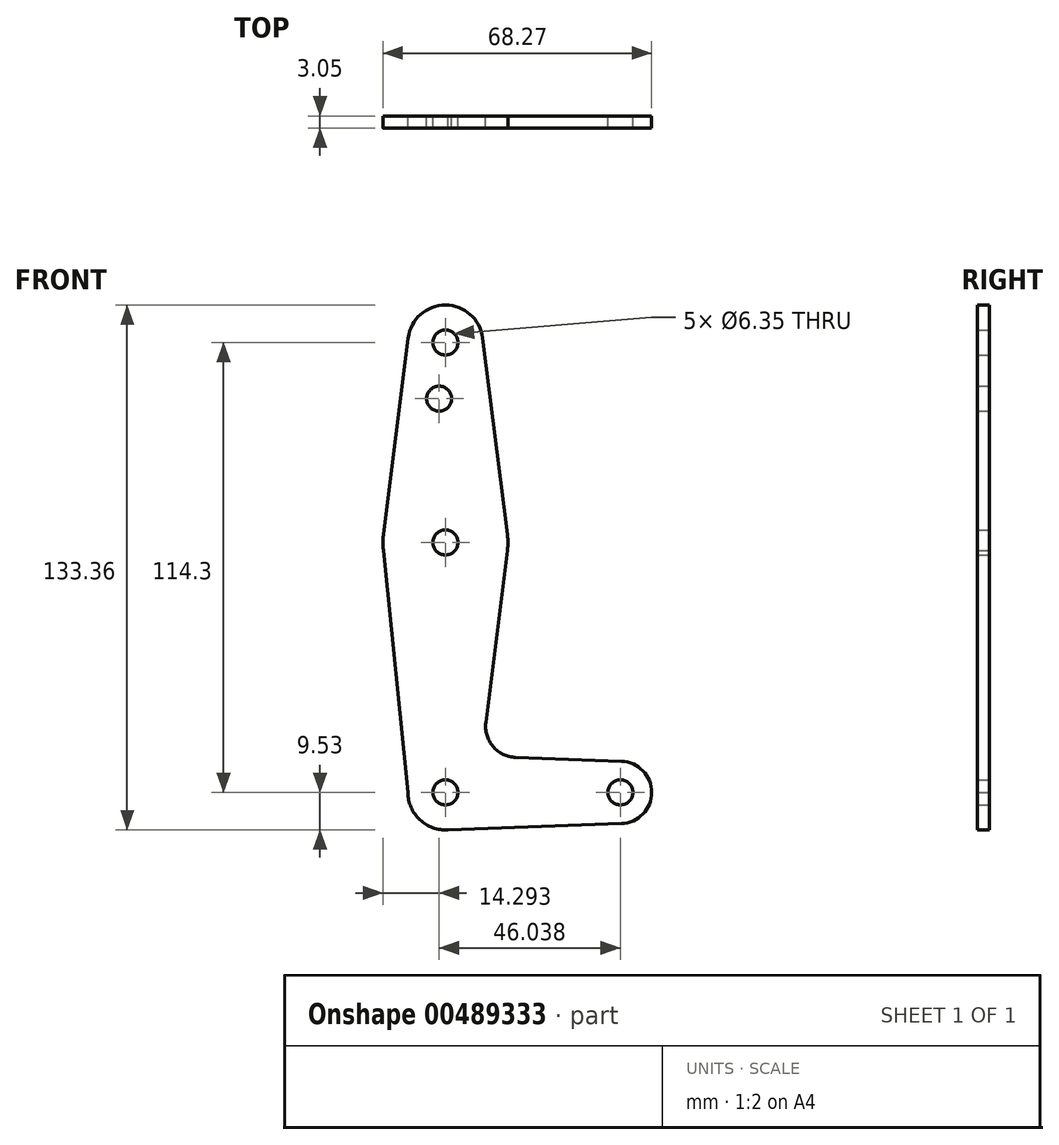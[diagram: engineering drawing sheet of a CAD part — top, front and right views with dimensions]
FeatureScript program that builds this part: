
annotation { "Feature Type Name" : "Feature", "Feature Type Description" : "" }
export const myFeature = defineFeature(function(context is Context, id is Id, definition is map)
    precondition{}
    {
        {
            var Q0;
            Q0=qCreatedBy(makeId("Front.planeOp"),FACE);
            var sketch = newSketch(context, id + "F0", { "sketchPlane" : qUnion([Q0])});
            skLineSegment(sketch, "E0", {"start": v(0, 0) * mm, "end": v(0, 114.3) * mm, "construction": true});
            skLineSegment(sketch, "E1", {"start": v(44.45, 0) * mm, "end": v(0, 0) * mm, "construction": true});
            skCircle(sketch, "E2", {"center": v(0, 0) * mm, "radius": 9.53 * mm});
            skCircle(sketch, "E3", {"center": v(0, 63.5) * mm, "radius": 15.88 * mm});
            skCircle(sketch, "E4", {"center": v(0, 114.3) * mm, "radius": 9.53 * mm});
            skCircle(sketch, "E5", {"center": v(44.45, 0) * mm, "radius": 7.94 * mm});
            skLineSegment(sketch, "E6", {"start": v(9.45, 115.5) * mm, "end": v(15.75, 65.48) * mm});
            skLineSegment(sketch, "E7", {"start": v(0, -9.52) * mm, "end": v(44.73, -7.93) * mm});
            skLineSegment(sketch, "E8", {"start": v(-9.45, 115.5) * mm, "end": v(-15.75, 65.48) * mm});
            skLineSegment(sketch, "E9", {"start": v(15.75, 61.52) * mm, "end": v(10.25, 17.83) * mm});
            skLineSegment(sketch, "E10", {"start": v(-15.75, 61.52) * mm, "end": v(-9.53, 0) * mm});
            skLineSegment(sketch, "E11", {"start": v(17.85, 8.9) * mm, "end": v(44.73, 7.93) * mm});
            skCircle(sketch, "E12", {"center": v(44.45, 0) * mm, "radius": 3.18 * mm});
            skCircle(sketch, "E13", {"center": v(0, 63.5) * mm, "radius": 3.18 * mm});
            skCircle(sketch, "E14", {"center": v(0, 114.3) * mm, "radius": 3.18 * mm});
            skCircle(sketch, "E15", {"center": v(0, 0) * mm, "radius": 3.18 * mm});
            skCircle(sketch, "E16", {"center": v(-1.59, 100.03) * mm, "radius": 3.18 * mm});
            skArc(sketch, "E17.filletArc", {"start": v(10.25, 17.83) * mm, "mid": v(12.08, 11.69) * mm, "end": v(17.85, 8.9) * mm});
            skSolve(sketch);
        }
        {
            var Q0;
            Q0 = qSketchRegion(id + "F0", true);
            extrude(context, id + "F1", {"entities" : qUnion([Q0]), "depth" : 3.05 * mm});
        }
    });
